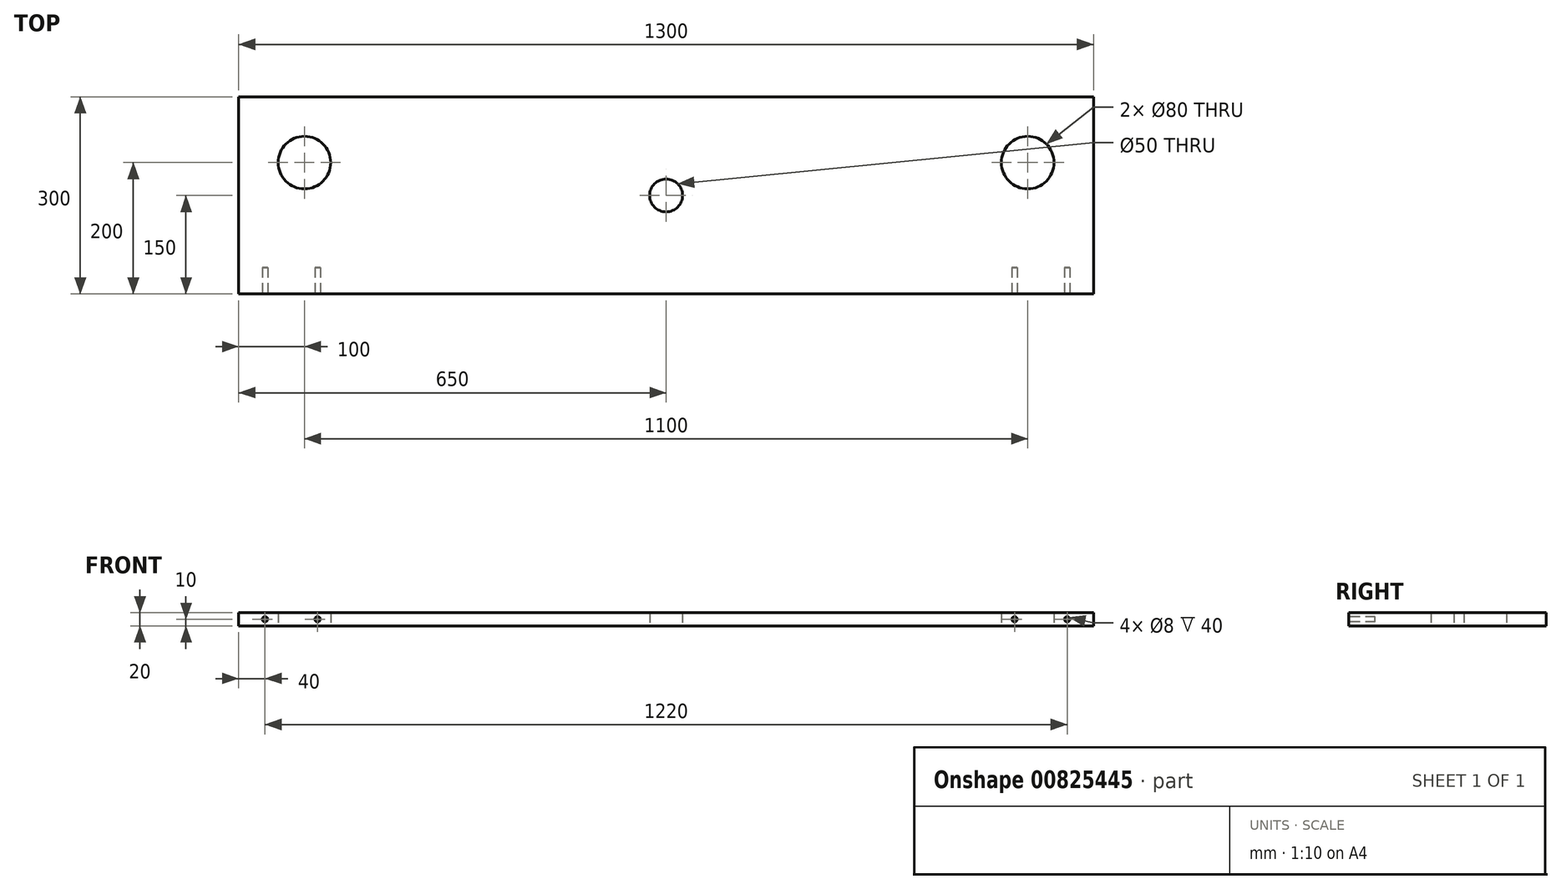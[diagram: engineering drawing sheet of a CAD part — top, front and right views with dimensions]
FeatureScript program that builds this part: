
annotation { "Feature Type Name" : "Feature", "Feature Type Description" : "" }
export const myFeature = defineFeature(function(context is Context, id is Id, definition is map)
    precondition{}
    {
        {
            var Q0;
            Q0=qCreatedBy(makeId("Top.planeOp"),FACE);
            var sketch = newSketch(context, id + "F0", { "sketchPlane" : qUnion([Q0])});
            skLineSegment(sketch, "E0.bottom", {"start": v(0, 300) * mm, "end": v(1300, 300) * mm});
            skLineSegment(sketch, "E0.top", {"start": v(0, 0) * mm, "end": v(1300, 0) * mm});
            skLineSegment(sketch, "E0.left", {"start": v(0, 300) * mm, "end": v(0, 0) * mm});
            skLineSegment(sketch, "E0.right", {"start": v(1300, 300) * mm, "end": v(1300, 0) * mm});
            skLineSegment(sketch, "E1", {"start": v(650, 300) * mm, "end": v(650, 0) * mm, "construction": true});
            skLineSegment(sketch, "E2", {"start": v(0, 150) * mm, "end": v(1300, 150) * mm, "construction": true});
            skCircle(sketch, "E3", {"center": v(650, 150) * mm, "radius": 25 * mm});
            skCircle(sketch, "E4", {"center": v(100, 200) * mm, "radius": 40 * mm});
            skCircle(sketch, "E5", {"center": v(1200, 200) * mm, "radius": 40 * mm});
            skSolve(sketch);
        }
        {
            var Q0;
            Q0=makeQuery(id+"F0.imprint","IMPRINT",FACE,{"disambiguationData":[TD([[makeQuery(id+"F0.imprint","IMPRINT",EDGE,{"derivedFrom":sQuery(id+"F0.wireOp",EDGE,"E0.bottom")}),-1.0]])]});
            extrude(context, id + "F1", {"entities" : qUnion([Q0]), "depth" : 20 * mm, "offsetDistance" : 25 * mm});
        }
        {
            var Q0;
            Q0=makeQuery(id+"F1.opExtrude","SWEPT_FACE",FACE,{"disambiguationData":[OSD([sQuery(id+"F0.wireOp",EDGE,"E0.top")])]});
            var sketch = newSketch(context, id + "F2", { "sketchPlane" : qUnion([Q0])});
            skLineSegment(sketch, "E6", {"start": v(0, 10) * mm, "end": v(1300, 10) * mm, "construction": true});
            skLineSegment(sketch, "E7", {"start": v(650, 20) * mm, "end": v(650, 0) * mm, "construction": true});
            skCircle(sketch, "E8", {"center": v(40, 10) * mm, "radius": 4 * mm});
            skCircle(sketch, "E9", {"center": v(120, 10) * mm, "radius": 4 * mm});
            skCircle(sketch, "E10.MirrorC", {"center": v(1260, 10) * mm, "radius": 4 * mm});
            skCircle(sketch, "E11.MirrorC", {"center": v(1180, 10) * mm, "radius": 4 * mm});
            skSolve(sketch);
        }
        {
            var Q0;
            Q0 = qSketchRegion(id + "F2", true);
            extrude(context, id + "F3", {"entities" : qUnion([Q0]), "operationType" : NewBodyOperationType.REMOVE, "oppositeDirection" : true, "depth" : 40 * mm, "offsetDistance" : 25 * mm});
        }
    });
